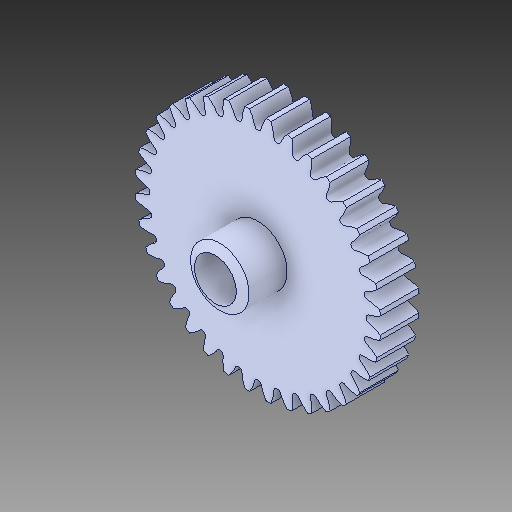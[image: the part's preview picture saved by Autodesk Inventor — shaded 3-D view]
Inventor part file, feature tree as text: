
AUTODESK INVENTOR PART (.ipt)
format: ipt  version: 2017 (Build 210142000, 142)  size: 508,416 bytes
history: native  units: in
note: dims shown in document units (in); Inventor stores cm internally (conversion verified against a paired STEP export)
features: chamfer x1
ambient origin geometry x8: Origin, YZ Plane, XZ Plane, XY Plane, X Axis, Y Axis, Z Axis, Center Point
bodies: Solid1 (feature_tree)
feature tree (1):
  chamfer  "Chamfer1"  [1 undecoded]
note: 1 required parameter value undecoded (feature->parameter linkage not recoverable at this tier; creation-order binding heuristic only, values carry confidence <= 0.55)
